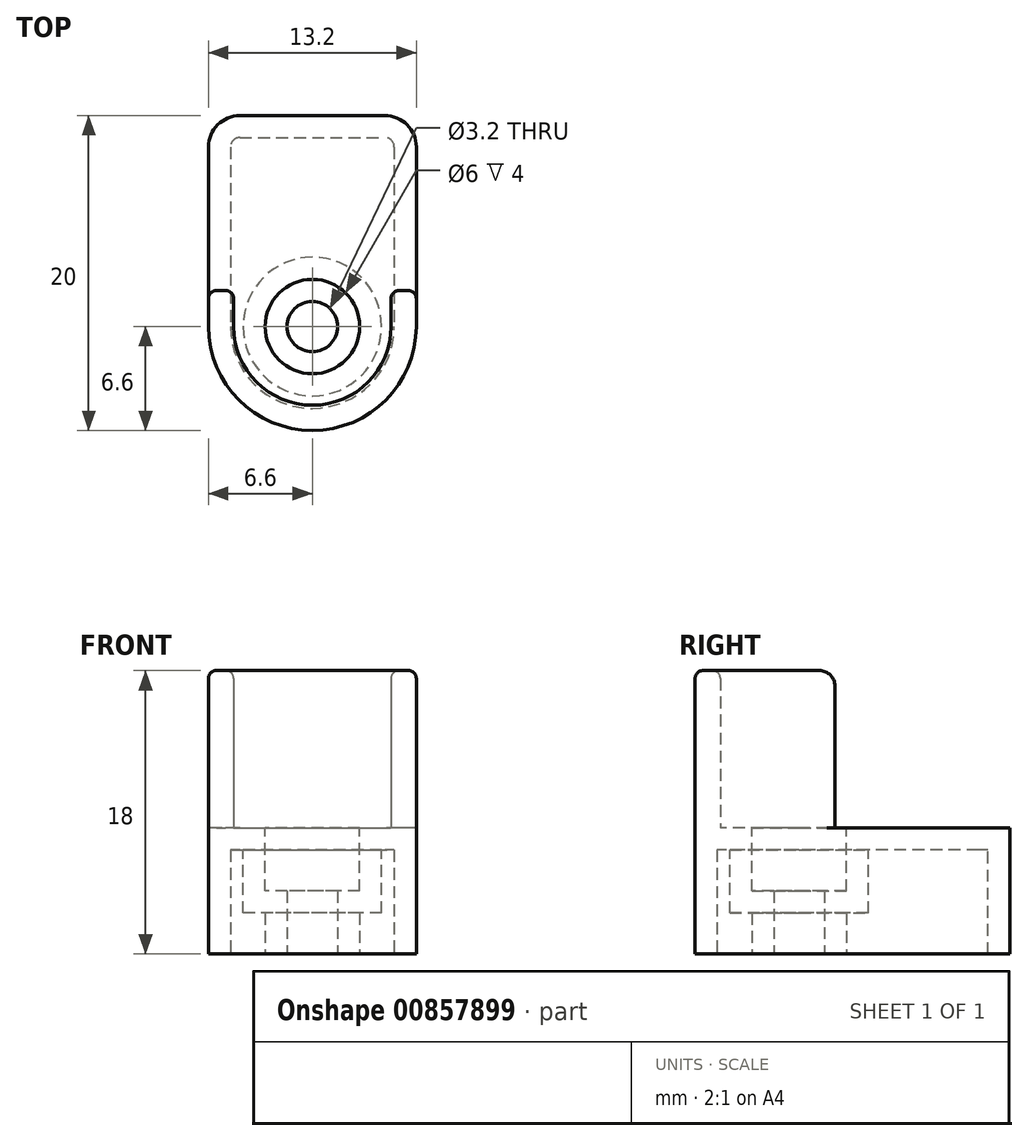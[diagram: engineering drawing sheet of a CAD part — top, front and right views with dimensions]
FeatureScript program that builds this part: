
annotation { "Feature Type Name" : "Feature", "Feature Type Description" : "" }
export const myFeature = defineFeature(function(context is Context, id is Id, definition is map)
    precondition{}
    {
        {
            var Q0;
            Q0=qCreatedBy(makeId("Top.planeOp"),FACE);
            var sketch = newSketch(context, id + "F0", { "sketchPlane" : qUnion([Q0])});
            skCircle(sketch, "E0", {"center": v(0, 0) * mm, "radius": 1.6 * mm});
            skLineSegment(sketch, "E1", {"start": v(-6.6, 13.4) * mm, "end": v(6.6, 13.4) * mm});
            skLineSegment(sketch, "E2", {"start": v(-6.6, 13.4) * mm, "end": v(-6.6, 0) * mm});
            skLineSegment(sketch, "E3", {"start": v(6.6, 13.4) * mm, "end": v(6.6, 0) * mm});
            skArc(sketch, "E4", {"start": v(-6.6, 0) * mm, "mid": v(0, -6.6) * mm, "end": v(6.6, 0) * mm});
            skSolve(sketch);
        }
        {
            var Q0;
            Q0=makeQuery(id+"F0.imprint","IMPRINT",FACE,{"disambiguationData":[TD([[makeQuery(id+"F0.imprint","IMPRINT",EDGE,{"derivedFrom":sQuery(id+"F0.wireOp",EDGE,"E0")}),-1.0]])]});
            extrude(context, id + "F1", {"entities" : qUnion([Q0]), "depth" : 8 * mm, "offsetDistance" : 25.4 * mm});
        }
        {
            var Q0;
            Q0=makeQuery(id+"F1.opExtrude","CAP_FACE",FACE,{"disambiguationData":[OSD([sQuery(id+"F0.wireOp",EDGE,"E0"),sQuery(id+"F0.wireOp",EDGE,"E1"),sQuery(id+"F0.wireOp",EDGE,"E2"),sQuery(id+"F0.wireOp",EDGE,"E3"),sQuery(id+"F0.wireOp",EDGE,"E4")])],"isStart":false});
            var sketch = newSketch(context, id + "F2", { "sketchPlane" : qUnion([Q0])});
            skArc(sketch, "E5.0", {"start": v(-6.6, 0) * mm, "mid": v(0, -6.6) * mm, "end": v(6.6, 0) * mm});
            skArc(sketch, "E6", {"start": v(-5, 0) * mm, "mid": v(0, -5) * mm, "end": v(5, 0) * mm});
            skLineSegment(sketch, "E7", {"start": v(-6.6, 0) * mm, "end": v(-6.6, 2.28) * mm});
            skLineSegment(sketch, "E8", {"start": v(-6.6, 2.28) * mm, "end": v(-5, 2.28) * mm});
            skLineSegment(sketch, "E9", {"start": v(-5, 0) * mm, "end": v(-5, 2.28) * mm});
            skLineSegment(sketch, "E10.MirrorCS", {"start": v(6.6, 2.28) * mm, "end": v(5, 2.28) * mm});
            skLineSegment(sketch, "E11.MirrorCS", {"start": v(5, 0) * mm, "end": v(5, 2.28) * mm});
            skLineSegment(sketch, "E12", {"start": v(6.6, 0) * mm, "end": v(6.6, 2.28) * mm});
            skSolve(sketch);
        }
        {
            var Q0;
            Q0=makeQuery(id+"F2.imprint","IMPRINT",FACE,{"disambiguationData":[TD([[makeQuery(id+"F2.imprint","IMPRINT",EDGE,{"derivedFrom":sQuery(id+"F2.wireOp",EDGE,"E5.0")}),1.0]])]});
            extrude(context, id + "F3", {"entities" : qUnion([Q0]), "operationType" : NewBodyOperationType.ADD, "depth" : 10 * mm, "offsetDistance" : 25 * mm});
        }
        {
            var Q0;
            Q0=makeQuery(id+"F3.opExtrude","CAP_EDGE",EDGE,{"disambiguationData":[OSD([sQuery(id+"F2.wireOp",EDGE,"E8")])],"isStart":false});
            var Q1;
            Q1=makeQuery(id+"F3.opExtrude","CAP_EDGE",EDGE,{"disambiguationData":[OSD([sQuery(id+"F2.wireOp",EDGE,"E10.MirrorCS")])],"isStart":false});
            fillet(context, id + "F4", {"entities" : qUnion([Q0, Q1]), "radius" : 1 * mm, "tangentPropagation" : true, "allowEdgeOverflow" : false});
        }
        {
            var Q0;
            Q0=makeQuery(id+"F3.opExtrude","SWEPT_EDGE",EDGE,{"disambiguationData":[OSD([sQuery(id+"F2.wireOp",EDGE,"E8"),sQuery(id+"F2.wireOp",EDGE,"E9")])]});
            var Q1;
            Q1=makeQuery(id+"F3.opExtrude","SWEPT_EDGE",EDGE,{"disambiguationData":[OSD([sQuery(id+"F0.wireOp",EDGE,"E2"),sQuery(id+"F2.wireOp",EDGE,"E7"),sQuery(id+"F2.wireOp",EDGE,"E8")])]});
            fillet(context, id + "F5", {"entities" : qUnion([Q0, Q1]), "radius" : .5 * mm, "tangentPropagation" : true, "allowEdgeOverflow" : false});
        }
        {
            var Q0;
            Q0=makeQuery(id+"F1.opExtrude","CAP_FACE",FACE,{"disambiguationData":[OSD([sQuery(id+"F0.wireOp",EDGE,"E0"),sQuery(id+"F0.wireOp",EDGE,"E1"),sQuery(id+"F0.wireOp",EDGE,"E2"),sQuery(id+"F0.wireOp",EDGE,"E3"),sQuery(id+"F0.wireOp",EDGE,"E4")])],"isStart":false});
            var sketch = newSketch(context, id + "F6", { "sketchPlane" : qUnion([Q0])});
            skCircle(sketch, "E13", {"center": v(0, 0) * mm, "radius": 3 * mm});
            skSolve(sketch);
        }
        {
            var Q0;
            Q0=makeQuery(id+"F6.imprint","IMPRINT",FACE,{"disambiguationData":[TD([[makeQuery(id+"F6.imprint","IMPRINT",EDGE,{"derivedFrom":sQuery(id+"F6.wireOp",EDGE,"E13")}),1.0]])]});
            var Q1;
            Q1=sQuery(id+"F6.wireOp",EDGE,"E13");
            extrude(context, id + "F7", {"entities" : qUnion([Q0]), "operationType" : NewBodyOperationType.REMOVE, "surfaceEntities" : qUnion([Q1]), "oppositeDirection" : true, "depth" : 4 * mm, "offsetDistance" : 25 * mm});
        }
        {
            var Q0;
            Q0=makeQuery(id+"F1.opExtrude","SWEPT_EDGE",EDGE,{"disambiguationData":[OSD([sQuery(id+"F0.wireOp",EDGE,"E1"),sQuery(id+"F0.wireOp",EDGE,"E3")])]});
            var Q1;
            Q1=makeQuery(id+"F1.opExtrude","SWEPT_EDGE",EDGE,{"disambiguationData":[OSD([sQuery(id+"F0.wireOp",EDGE,"E1"),sQuery(id+"F0.wireOp",EDGE,"E2")])]});
            fillet(context, id + "F8", {"entities" : qUnion([Q0, Q1]), "radius" : 2 * mm, "tangentPropagation" : true, "allowEdgeOverflow" : false});
        }
        {
            var Q0;
            Q0=makeQuery(id+"F1.opExtrude","CAP_FACE",FACE,{"disambiguationData":[OSD([sQuery(id+"F0.wireOp",EDGE,"E0"),sQuery(id+"F0.wireOp",EDGE,"E1"),sQuery(id+"F0.wireOp",EDGE,"E2"),sQuery(id+"F0.wireOp",EDGE,"E3"),sQuery(id+"F0.wireOp",EDGE,"E4")])],"isStart":true});
            shell(context, id + "F9", {"entities" : qUnion([Q0]), "thickness" : 1.4 * mm});
        }
    });
